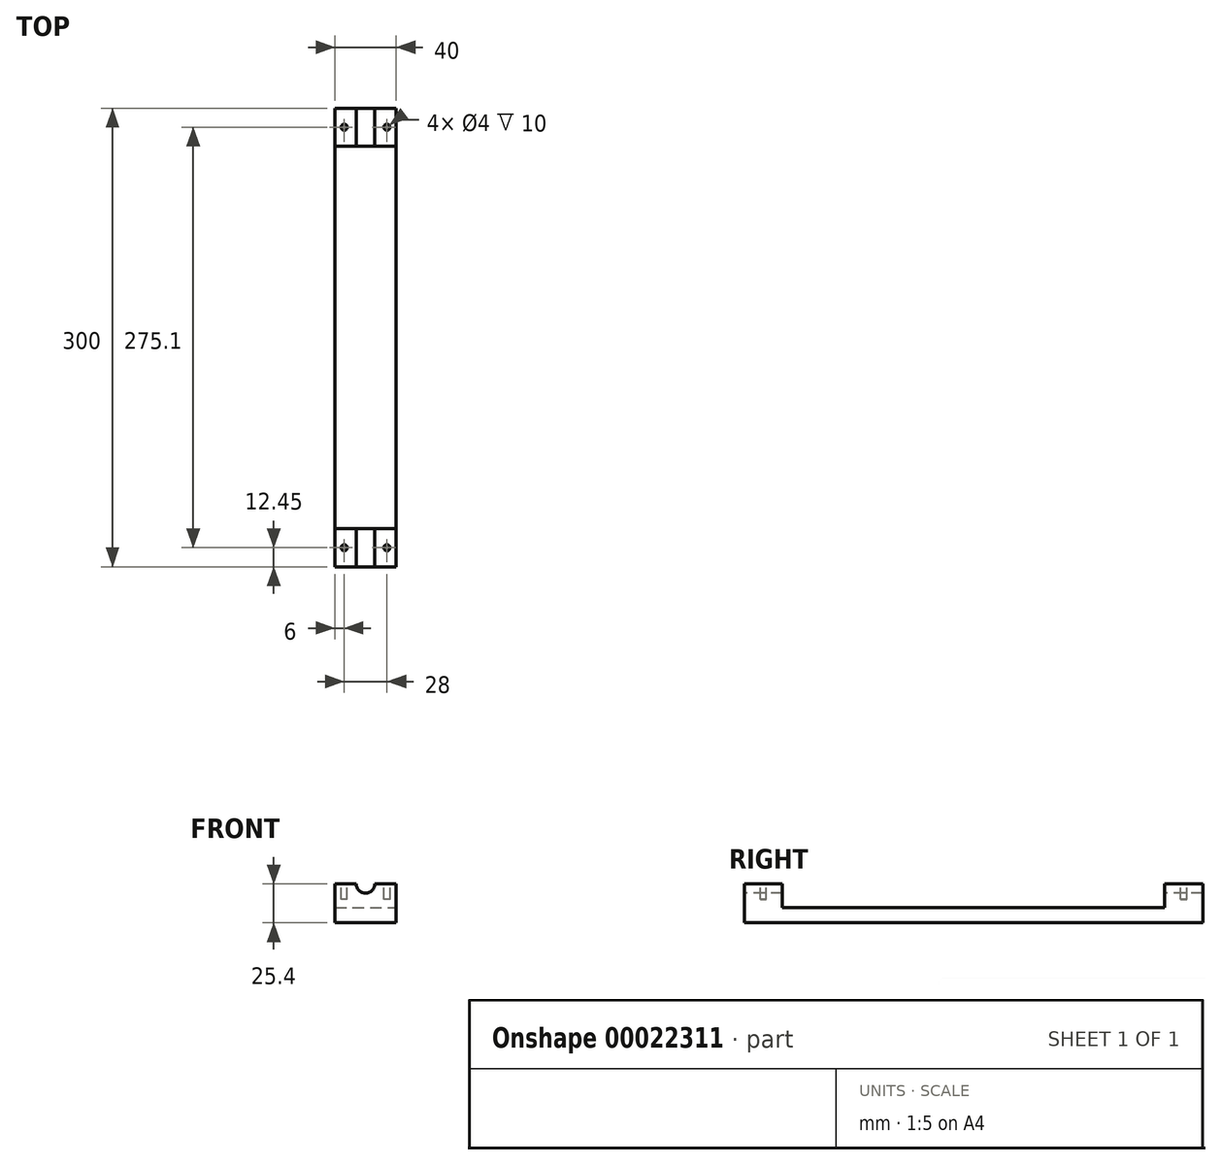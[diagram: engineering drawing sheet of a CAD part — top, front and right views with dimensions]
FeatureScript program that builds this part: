
annotation { "Feature Type Name" : "Feature", "Feature Type Description" : "" }
export const myFeature = defineFeature(function(context is Context, id is Id, definition is map)
    precondition{}
    {
        {
            var Q0;
            Q0=qCreatedBy(makeId("Front.planeOp"),FACE);
            var sketch = newSketch(context, id + "F0", { "sketchPlane" : qUnion([Q0])});
            skLineSegment(sketch, "E0.rect.bottom", {"start": v(-20, -12.7) * mm, "end": v(20, -12.7) * mm});
            skLineSegment(sketch, "E0.rect.left", {"start": v(-20, -12.7) * mm, "end": v(-20, 12.7) * mm});
            skLineSegment(sketch, "E0.rect.right", {"start": v(20, -12.7) * mm, "end": v(20, 12.7) * mm});
            skPoint(sketch, "E0.rect.middle", {"position": v(0, 0) * mm});
            skLineSegment(sketch, "E1", {"start": v(-20, 12.7) * mm, "end": v(20, 12.7) * mm});
            skSolve(sketch);
        }
        {
            var Q0;
            Q0=makeQuery(id+"F0.imprint","IMPRINT",FACE,{"disambiguationData":[TD([[makeQuery(id+"F0.imprint","IMPRINT",EDGE,{"derivedFrom":sQuery(id+"F0.wireOp",EDGE,"E0.rect.bottom")}),1.0]])]});
            extrude(context, id + "F1", {"entities" : qUnion([Q0]), "depth" : 300 * mm});
        }
        {
            var Q0;
            Q0=makeQuery(id+"F1.opExtrude","SWEPT_FACE",FACE,{"disambiguationData":[OSD([sQuery(id+"F0.wireOp",EDGE,"E0.rect.right")])]});
            var sketch = newSketch(context, id + "F2", { "sketchPlane" : qUnion([Q0])});
            skLineSegment(sketch, "E2.bottom", {"start": v(-24.9, 12.7) * mm, "end": v(-275.1, 12.7) * mm});
            skLineSegment(sketch, "E2.top", {"start": v(-24.9, -2.9) * mm, "end": v(-275.1, -2.9) * mm});
            skLineSegment(sketch, "E2.left", {"start": v(-24.9, 12.7) * mm, "end": v(-24.9, -2.9) * mm});
            skLineSegment(sketch, "E2.right", {"start": v(-275.1, 12.7) * mm, "end": v(-275.1, -2.9) * mm});
            skSolve(sketch);
        }
        {
            var Q0;
            Q0 = qSketchRegion(id + "F2", true);
            extrude(context, id + "F3", {"entities" : qUnion([Q0]), "operationType" : NewBodyOperationType.REMOVE, "endBound" : BoundingType.THROUGH_ALL, "oppositeDirection" : true, "depth" : 25 * mm});
        }
        {
            var Q0;
            Q0=makeQuery(id+"F1.opExtrude","CAP_FACE",FACE,{"disambiguationData":[OSD([sQuery(id+"F0.wireOp",EDGE,"E0.rect.bottom"),sQuery(id+"F0.wireOp",EDGE,"E0.rect.left"),sQuery(id+"F0.wireOp",EDGE,"E0.rect.right"),sQuery(id+"F0.wireOp",EDGE,"E1")])],"isStart":false});
            var sketch = newSketch(context, id + "F4", { "sketchPlane" : qUnion([Q0])});
            skCircle(sketch, "E3", {"center": v(0, 12.7) * mm, "radius": 6.05 * mm});
            skSolve(sketch);
        }
        {
            var Q0;
            {var subQ0=makeQuery(id+"F1.opExtrude","CAP_EDGE",EDGE,{"disambiguationData":[OSD([sQuery(id+"F0.wireOp",EDGE,"E1")])],"isStart":false});var subQ1=sQuery(id+"F4.wireOp",EDGE,"E3");var subQ3=makeQuery(id+"F4.imprint","INTERSECT",VERTEX,{"disambiguationData":[OD(0.0)],"derivedFrom":[subQ0,subQ1]});Q0=makeQuery(id+"F4.imprint","IMPRINT",FACE,{"disambiguationData":[TD([[makeQuery(id+"F4.imprint","IMPRINT",EDGE,{"disambiguationData":[TD([[subQ3,-1.0]])],"derivedFrom":subQ1}),1.0]])]});}
            extrude(context, id + "F5", {"entities" : qUnion([Q0]), "operationType" : NewBodyOperationType.REMOVE, "endBound" : BoundingType.THROUGH_ALL, "oppositeDirection" : true, "depth" : 25 * mm});
        }
        {
            var Q0;
            {var subQ0=sQuery(id+"F0.wireOp",EDGE,"E1");var subQ1=makeQuery(id+"F3.opExtrude","SWEPT_FACE",FACE,{"disambiguationData":[OSD([sQuery(id+"F2.wireOp",EDGE,"E2.right")])]});var subQ3=sQuery(id+"F0.wireOp",EDGE,"E0.rect.left");var subQ4=makeQuery(id+"F1.opExtrude","SWEPT_FACE",FACE,{"disambiguationData":[OSD([subQ3])]});Q0=makeQuery(id+"F5.boolean.opBoolean","SPLIT",FACE,{"disambiguationData":[TD([subQ4])],"derivedFrom":makeQuery(id+"F3.boolean.opBoolean","SPLIT",FACE,{"disambiguationData":[TD([subQ1])],"derivedFrom":makeQuery(id+"F1.opExtrude","SWEPT_FACE",FACE,{"disambiguationData":[OSD([subQ0])]})})});}
            var sketch = newSketch(context, id + "F6", { "sketchPlane" : qUnion([Q0])});
            skCircle(sketch, "E4", {"center": v(-14, -287.55) * mm, "radius": 2 * mm});
            skCircle(sketch, "E5", {"center": v(14, -287.55) * mm, "radius": 2 * mm});
            skLineSegment(sketch, "E6", {"start": v(-14, -287.55) * mm, "end": v(14, -287.55) * mm, "construction": true});
            skCircle(sketch, "E7", {"center": v(-14, -12.45) * mm, "radius": 2 * mm});
            skCircle(sketch, "E8", {"center": v(14, -12.45) * mm, "radius": 2 * mm});
            skLineSegment(sketch, "E9", {"start": v(-14, -12.45) * mm, "end": v(14, -12.45) * mm, "construction": true});
            skSolve(sketch);
        }
        {
            var Q0;
            Q0 = qSketchRegion(id + "F6", true);
            extrude(context, id + "F7", {"entities" : qUnion([Q0]), "operationType" : NewBodyOperationType.REMOVE, "oppositeDirection" : true, "depth" : 10 * mm});
        }
        {
            var Q0;
            Q0=makeQuery(id+"F3.boolean.opBoolean","COPY",FACE,{"derivedFrom":makeQuery(id+"F3.opExtrude","SWEPT_FACE",FACE,{"disambiguationData":[OSD([sQuery(id+"F2.wireOp",EDGE,"E2.right")])]})});
            cPlane(context, id + "F8", {"entities" : qUnion([Q0]), "cplaneType" : CPlaneType.OFFSET, "offset" : (250.2 / 2) * mm, "width" : 150 * mm, "height" : 150 * mm});
        }
    });
